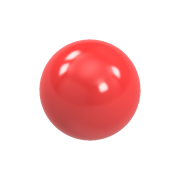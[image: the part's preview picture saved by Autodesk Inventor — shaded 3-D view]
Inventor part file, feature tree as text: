
AUTODESK INVENTOR PART (.ipt)
format: ipt  version: 2020 (Build 240168000, 168)  size: 110,592 bytes
history: native  units: mm
features: revolve x1, sketch x1
ambient origin geometry x8: Origin, YZ Plane, XZ Plane, XY Plane, X Axis, Y Axis, Z Axis, Center Point
bodies: Solid1 (feature_tree)
feature tree (2):
  revolve  "Revolution1"  Angle=90.0deg
  sketch  "Sketch1"  dims[d0=15.0mm d1=90.0deg]
